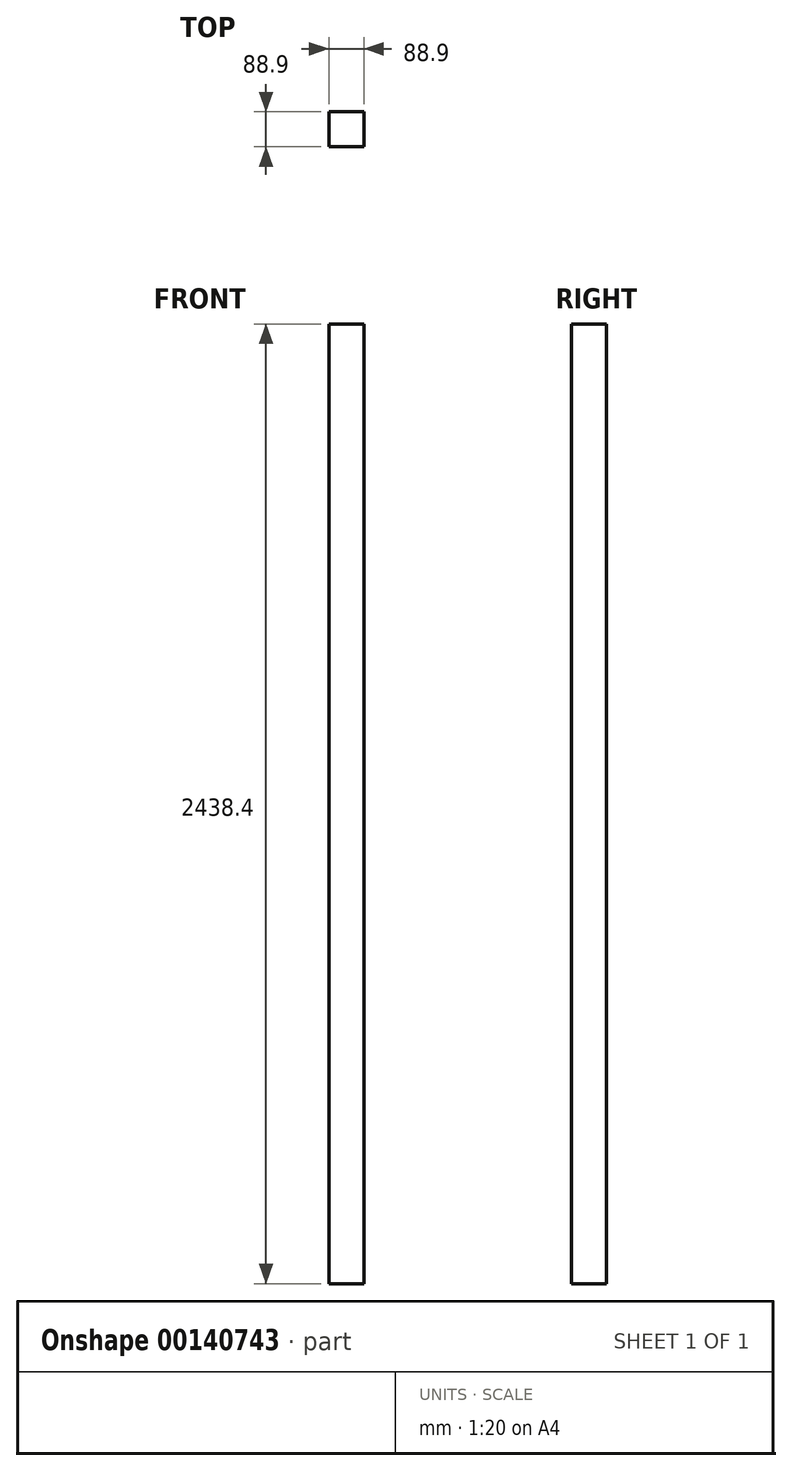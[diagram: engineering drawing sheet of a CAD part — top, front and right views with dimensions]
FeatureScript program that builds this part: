
annotation { "Feature Type Name" : "Feature", "Feature Type Description" : "" }
export const myFeature = defineFeature(function(context is Context, id is Id, definition is map)
    precondition{}
    {
        {
            var Q0;
            Q0=qCreatedBy(makeId("Top.planeOp"),FACE);
            var sketch = newSketch(context, id + "F0", { "sketchPlane" : qUnion([Q0])});
            skLineSegment(sketch, "E0.bottom", {"start": v(44.45, 44.45) * mm, "end": v(-44.45, 44.45) * mm});
            skLineSegment(sketch, "E0.top", {"start": v(44.45, -44.45) * mm, "end": v(-44.45, -44.45) * mm});
            skLineSegment(sketch, "E0.left", {"start": v(44.45, 44.45) * mm, "end": v(44.45, -44.45) * mm});
            skLineSegment(sketch, "E0.right", {"start": v(-44.45, 44.45) * mm, "end": v(-44.45, -44.45) * mm});
            skPoint(sketch, "E0.middle", {"position": v(0, 0) * mm});
            skSolve(sketch);
        }
        {
            var Q0;
            Q0=makeQuery(id+"F0.imprint","IMPRINT",FACE,{"disambiguationData":[TD([[makeQuery(id+"F0.imprint","IMPRINT",EDGE,{"derivedFrom":sQuery(id+"F0.wireOp",EDGE,"E0.bottom")}),1.0]])]});
            extrude(context, id + "F1", {"entities" : qUnion([Q0]), "depth" : 2438.4 * mm});
        }
    });
